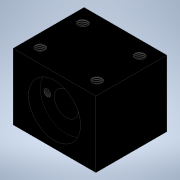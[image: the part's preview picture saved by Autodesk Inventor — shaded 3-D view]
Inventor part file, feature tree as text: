
AUTODESK INVENTOR PART (.ipt)
format: ipt  version: 2020 (Build 240168000, 168)  size: 172,544 bytes
history: native  units: mm
features: thread x6, extrude x5, sketch x5
ambient origin geometry x8: Origin, YZ Plane, XZ Plane, XY Plane, X Axis, Y Axis, Z Axis, Center Point
bodies: Solid1 (feature_tree)
feature tree (16):
  extrude  "Extrusion1"  Depth=28.0mm
  extrude  "Extrusion2"  Depth=30.0mm TaperAngle=0.0deg
  extrude  "Extrusion4"  Depth=14.0mm
  thread  "Thread7"  [1 undecoded]
  thread  "Thread8"  [1 undecoded]
  thread  "Thread9"  [1 undecoded]
  thread  "Thread10"  [1 undecoded]
  extrude  "Extrusion5"  Depth=15.0mm
  extrude  "Extrusion6"  Depth=10.0mm TaperAngle=0.0deg
  thread  "Thread11"  [1 undecoded]
  thread  "Thread12"  [1 undecoded]
  sketch  "Sketch1"  dims[d0=17.5mm d1=28.0mm]
  sketch  "Sketch2"  dims[d2=35.0mm d3=30.0mm d4=0.0mm]
  sketch  "Sketch4"  dims[d5=10.2mm d6=14.0mm d7=30.0mm d8=0.0mm d37=17.5mm d38=4.0mm d39=4.0mm]
  sketch  "Sketch7"  dims[d42=15.0mm d43=4.0mm]
  sketch  "Sketch9"  dims[d44=4.0mm d51=10.0mm d52=0.0mm d57=10.0mm d58=0.0mm d59=10.0mm d60=0.0mm d61=6.0mm d62=6.0mm d63=6.0mm d64=6.0mm d67=10.0mm d68=0.0mm d69=10.0mm d70=0.0mm d72=22.0mm d73=5.0mm d74=0.0mm d76=3.0mm d78=3.0mm d79=10.0mm d80=0.0mm d81=10.0mm d82=0.0mm d83=10.0mm d84=0.0mm d85=17.5mm d86=12.0mm d87=12.0mm d88=12.0mm d89=12.0mm]
note: 6 required parameter values undecoded (feature->parameter linkage not recoverable at this tier; creation-order binding heuristic only, values carry confidence <= 0.55)
